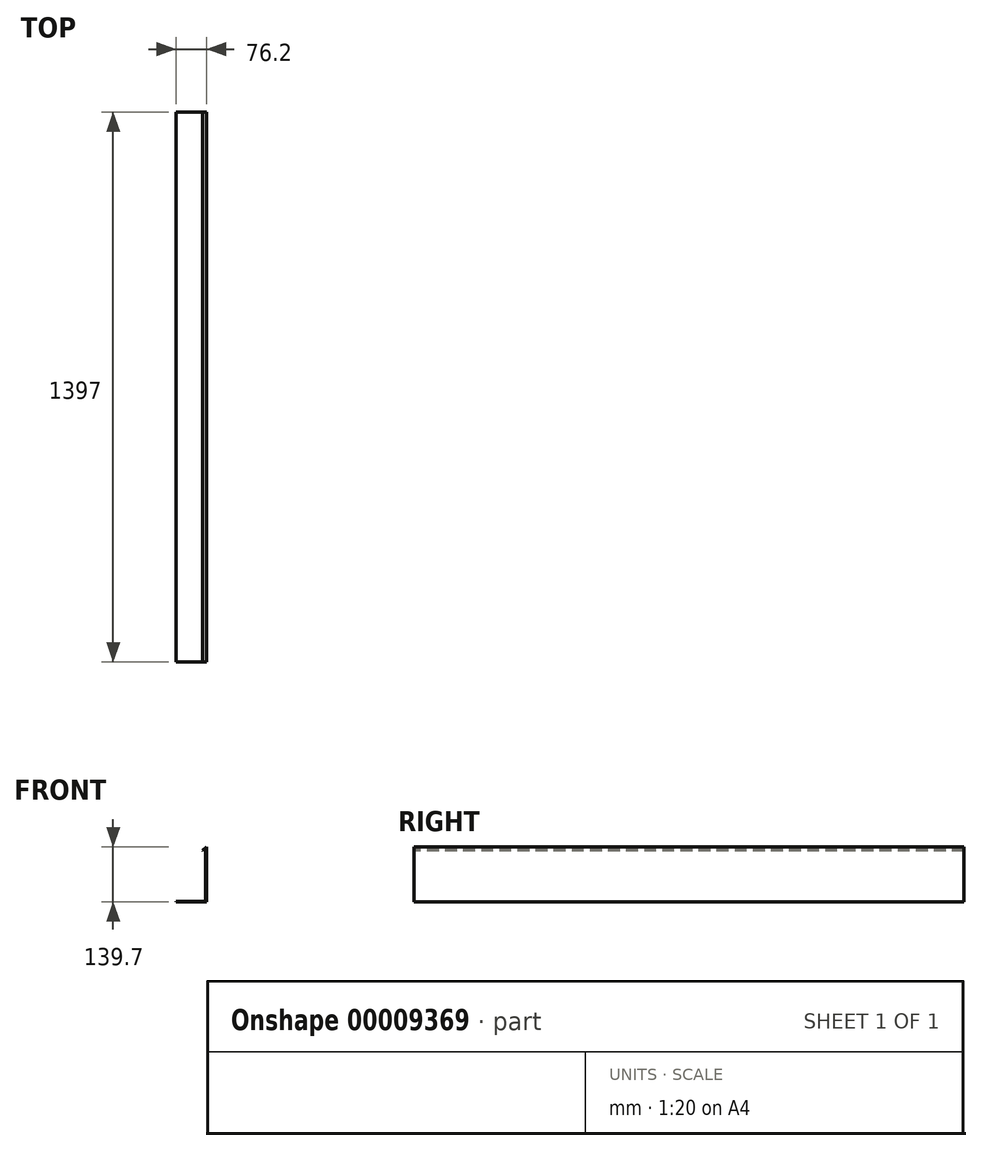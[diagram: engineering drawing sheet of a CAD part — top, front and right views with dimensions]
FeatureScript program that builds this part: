
annotation { "Feature Type Name" : "Feature", "Feature Type Description" : "" }
export const myFeature = defineFeature(function(context is Context, id is Id, definition is map)
    precondition{}
    {
        {
            var Q0;
            Q0=qCreatedBy(makeId("Front.planeOp"),FACE);
            var sketch = newSketch(context, id + "F0", { "sketchPlane" : qUnion([Q0])});
            skLineSegment(sketch, "E0", {"start": v(8.98, 130.72) * mm, "end": v(0, 139.7) * mm});
            skLineSegment(sketch, "E1", {"start": v(0, 139.7) * mm, "end": v(0, 0) * mm});
            skLineSegment(sketch, "E2", {"start": v(0, 0) * mm, "end": v(76.2, 0) * mm});
            skLineSegment(sketch, "E3", {"start": v(76.2, 0) * mm, "end": v(76.2, 1.31) * mm});
            skLineSegment(sketch, "E4", {"start": v(76.2, 1.31) * mm, "end": v(1.31, 1.31) * mm});
            skLineSegment(sketch, "E5", {"start": v(1.31, 1.31) * mm, "end": v(1.31, 136.54) * mm});
            skLineSegment(sketch, "E6", {"start": v(1.31, 136.54) * mm, "end": v(8.05, 129.8) * mm});
            skLineSegment(sketch, "E7", {"start": v(8.05, 129.8) * mm, "end": v(8.98, 130.72) * mm});
            skSolve(sketch);
        }
        {
            var Q0;
            Q0=makeQuery(id+"F0.imprint","IMPRINT",FACE,{"disambiguationData":[TD([[makeQuery(id+"F0.imprint","IMPRINT",EDGE,{"derivedFrom":sQuery(id+"F0.wireOp",EDGE,"E0")}),1.0]])]});
            extrude(context, id + "F1", {"entities" : qUnion([Q0]), "depth" : 1397 * mm});
        }
        {
            var Q0;
            Q0=makeQuery(id+"F1.opExtrude","SWEPT_BODY",BODY,{"disambiguationData":[OSD([sQuery(id+"F0.wireOp",EDGE,"E0"),sQuery(id+"F0.wireOp",EDGE,"E1"),sQuery(id+"F0.wireOp",EDGE,"E2"),sQuery(id+"F0.wireOp",EDGE,"E3"),sQuery(id+"F0.wireOp",EDGE,"E4"),sQuery(id+"F0.wireOp",EDGE,"E5"),sQuery(id+"F0.wireOp",EDGE,"E6"),sQuery(id+"F0.wireOp",EDGE,"E7")])]});
            var Q1;
            Q1=sQuery(id+"F0.wireOp",EDGE,"E1");
            var Q2;
            Q2=sQuery(id+"F0.wireOp",EDGE,"E1");
            transform(context, id + "F2", {"entities" : qUnion([Q0]), "transformType" : TransformType.ROTATION, "transformAxis" : qUnion([Q2]), "angle" : 180 * degree, "makeCopy" : false});
        }
    });
